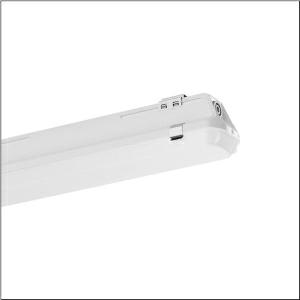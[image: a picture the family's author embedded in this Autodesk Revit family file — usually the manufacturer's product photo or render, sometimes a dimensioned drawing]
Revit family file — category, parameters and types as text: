
# Revit family: monsun_r__11_chemical_51fp30dp460h_97dc
name_source: partatom
category: Lighting Fixtures
units: mm (PartAtom-declared; Revit-internal decimal feet)

## family parameters
Cut with Voids When Loaded = No
Host = Face
Light Source = No
Part Type = Normal
Room Calculation Point = No
Round Connector Dimension = Use Diameter
Shared = No

## types (1)
- --- (1 x LED, 5730 lm, 34.6 W, 4000K)
    Apparent Load = 35 VA
    CIE Flux Codes = 48 77 93 95 100
    Color Rendering = 80
    Color Temperature = 4000K
    Default Elevation = 1800 mm
    Description = Monsun® 11 chemical, damp-proof luminaire, chain hanger, primary optical cover: enclosure, of PA, light emission: direct distribution, primary light characteristic: symmetric, installation type: suspended mounting, surface-mounted, horizontal mounting, vertical mounting, LED, rated luminous flux: 5.730lm, luminous efficacy: 166lm/W, light colour: 840, colour temperature: 4000K, control gear: ECG DALI, with terminal, 5-pole, max. 2.5mm², mains connection: 220..240V, AC, 50/60Hz, rated input power: 35W, luminaire housing, of glass-fibre reinforced polyester, uncoated, bright grey, incl. chain hanger, length: 1.590mm, width: 90mm, height: 88mm, clip for enclosure, of stainless steel (V2A), ceiling mounting element, of stainless steel (V2A), chain hanger, of stainless steel (V2A), protection rating (complete): IP66, insulation class (complete): insulation class I (protective earthing), certification: CE, ENEC, VDE, UKCA, protection symbol: D, impact resistance: IK08, permissible operating ambient temperature: -25..+40°C, standard: EN 50419, EN 60598-2-1, no direct snow, no direct sun, no direct rain, for indoor or canopied outdoor use, corresponds to IFS (International Featured Standards) requirements for safety and quality in the food industry, contact your sales advisor before using the luminaires in applications with unclear chemical exposure, large temperature fluctuations or condensation-forming humidity, LABS conformity tested according to VDMA 24364:2018-05, packaging unit: 1 piece
    Height = 89 mm
    Lamp = 1 x LED
    Lamp Light Flux = 5730 lm
    Lamp Power = 34.6 W
    Lamp count = 1
    Length = 1590 mm
    Luminous efficacy = 166 lm/W
    Manufacturer = Siteco
    ModVariant = No
    Model = 51FP30DP460H
    Mounting Place = Ceiling
    Mounting Type = Surface mounted
    Number of Poles = 1
    OnlyDefault = Yes
    Power Factor = 1
    Product Name = Monsun® 11 chemical
    Product group = damp-proof luminaire
    ProductGroupID = 300
    Protection Class = Protection class I
    Protection Degree = IP 66
    RLX_Detail_Level = 1
    RLX_Emergency_Light_Flux = 0 lm
    RLX_Emergency_Type = 0
    RLX_Emergency_Type_DB = No
    RlxData = <blob elided: 92385 chars, md5=e998a0ff>
    Socket = socket
    Standby Power = 0 W
    System Light Flux = 5730 lm
    System Power = 35 W
    Type Comments = factory setting: luminous flux: 100 % | dim-lin: 254 | 232 mA
    Type Image = l_1004748.jpg
    URL = http://relux.com
    VarID = @adj_142125
    Voltage = 0 V
    Weight = 0.00 kg
    Width = 90 mm

## geometry (parser evidence)
native form markers: Blend x4, Sweep x15
no freeform markers — native parametric forms only
